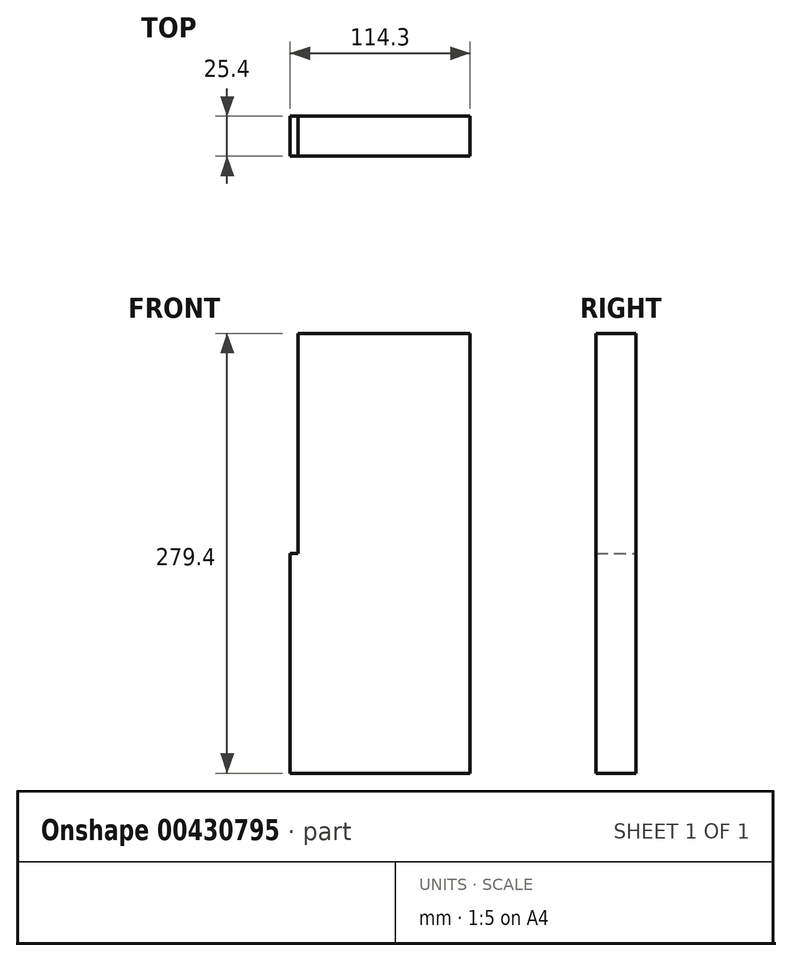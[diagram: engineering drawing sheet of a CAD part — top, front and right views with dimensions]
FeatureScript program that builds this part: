
annotation { "Feature Type Name" : "Feature", "Feature Type Description" : "" }
export const myFeature = defineFeature(function(context is Context, id is Id, definition is map)
    precondition{}
    {
        {
            var Q0;
            Q0=qCreatedBy(makeId("Front.planeOp"),FACE);
            var sketch = newSketch(context, id + "F0", { "sketchPlane" : qUnion([Q0])});
            skLineSegment(sketch, "E0.bottom", {"start": v(0, 0) * mm, "end": v(114.3, 0) * mm});
            skLineSegment(sketch, "E0.top", {"start": v(5.08, 279.4) * mm, "end": v(114.3, 279.4) * mm});
            skLineSegment(sketch, "E0.left", {"start": v(0, 0) * mm, "end": v(0, 139.7) * mm});
            skLineSegment(sketch, "E1.top", {"start": v(0, 139.7) * mm, "end": v(5.08, 139.7) * mm});
            skLineSegment(sketch, "E1.right", {"start": v(5.08, 279.4) * mm, "end": v(5.08, 139.7) * mm});
            skLineSegment(sketch, "E2", {"start": v(114.3, 279.4) * mm, "end": v(114.3, 0) * mm});
            skSolve(sketch);
        }
        {
            var Q0;
            Q0 = qSketchRegion(id + "F0", true);
            extrude(context, id + "F1", {"entities" : qUnion([Q0]), "depth" : 25.4 * mm});
        }
    });
